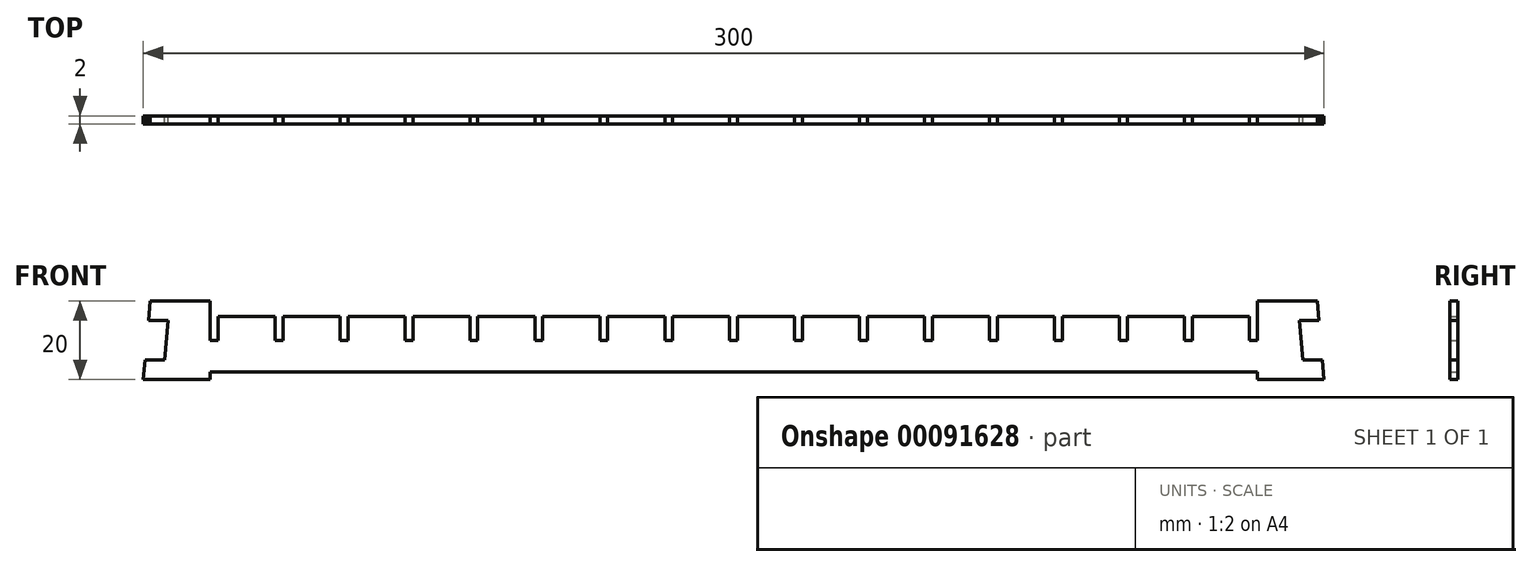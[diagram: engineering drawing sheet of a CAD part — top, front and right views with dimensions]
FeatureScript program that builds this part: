
annotation { "Feature Type Name" : "Feature", "Feature Type Description" : "" }
export const myFeature = defineFeature(function(context is Context, id is Id, definition is map)
    precondition{}
    {
        {
            var Q0;
            Q0=qCreatedBy(makeId("Front.planeOp"),FACE);
            var sketch = newSketch(context, id + "F0", { "sketchPlane" : qUnion([Q0])});
            skLineSegment(sketch, "E0", {"start": v(0, 0) * mm, "end": v(17, 0) * mm});
            skLineSegment(sketch, "E1", {"start": v(300, 0) * mm, "end": v(299.56, 5) * mm});
            skLineSegment(sketch, "E2", {"start": v(283, 20) * mm, "end": v(283, 10) * mm});
            skLineSegment(sketch, "E3", {"start": v(283, 10) * mm, "end": v(281, 10) * mm});
            skLineSegment(sketch, "E4", {"start": v(281, 10) * mm, "end": v(281, 16) * mm});
            skLineSegment(sketch, "E5", {"start": v(281, 16) * mm, "end": v(266.5, 16) * mm});
            skLineSegment(sketch, "E6", {"start": v(266.5, 16) * mm, "end": v(266.5, 10) * mm});
            skLineSegment(sketch, "E7", {"start": v(266.5, 10) * mm, "end": v(264.5, 10) * mm});
            skLineSegment(sketch, "E8", {"start": v(264.5, 10) * mm, "end": v(264.5, 16) * mm});
            skLineSegment(sketch, "E9", {"start": v(264.5, 16) * mm, "end": v(250, 16) * mm});
            skLineSegment(sketch, "E10", {"start": v(233.5, 16) * mm, "end": v(233.5, 10) * mm});
            skLineSegment(sketch, "E11", {"start": v(233.5, 10) * mm, "end": v(231.5, 10) * mm});
            skLineSegment(sketch, "E12", {"start": v(231.5, 10) * mm, "end": v(231.5, 16) * mm});
            skLineSegment(sketch, "E13", {"start": v(231.5, 16) * mm, "end": v(217, 16) * mm});
            skLineSegment(sketch, "E14", {"start": v(217, 16) * mm, "end": v(217, 10) * mm});
            skLineSegment(sketch, "E15", {"start": v(217, 10) * mm, "end": v(215, 10) * mm});
            skLineSegment(sketch, "E16", {"start": v(215, 10) * mm, "end": v(215, 16) * mm});
            skLineSegment(sketch, "E17", {"start": v(215, 16) * mm, "end": v(200.5, 16) * mm});
            skLineSegment(sketch, "E18", {"start": v(200.5, 16) * mm, "end": v(200.5, 10) * mm});
            skLineSegment(sketch, "E19", {"start": v(200.5, 10) * mm, "end": v(198.5, 10) * mm});
            skLineSegment(sketch, "E20", {"start": v(198.5, 10) * mm, "end": v(198.5, 16) * mm});
            skLineSegment(sketch, "E21", {"start": v(198.5, 16) * mm, "end": v(184, 16) * mm});
            skLineSegment(sketch, "E22", {"start": v(184, 16) * mm, "end": v(184, 10) * mm});
            skLineSegment(sketch, "E23", {"start": v(184, 10) * mm, "end": v(182, 10) * mm});
            skLineSegment(sketch, "E24", {"start": v(182, 10) * mm, "end": v(182, 16) * mm});
            skLineSegment(sketch, "E25", {"start": v(182, 16) * mm, "end": v(167.5, 16) * mm});
            skLineSegment(sketch, "E26", {"start": v(167.5, 16) * mm, "end": v(167.5, 10) * mm});
            skLineSegment(sketch, "E27", {"start": v(167.5, 10) * mm, "end": v(165.5, 10) * mm});
            skLineSegment(sketch, "E28", {"start": v(165.5, 10) * mm, "end": v(165.5, 16) * mm});
            skLineSegment(sketch, "E29", {"start": v(165.5, 16) * mm, "end": v(151, 16) * mm});
            skLineSegment(sketch, "E30", {"start": v(151, 16) * mm, "end": v(151, 10) * mm});
            skLineSegment(sketch, "E31", {"start": v(151, 10) * mm, "end": v(149, 10) * mm});
            skLineSegment(sketch, "E32", {"start": v(149, 10) * mm, "end": v(149, 16) * mm});
            skLineSegment(sketch, "E33", {"start": v(149, 16) * mm, "end": v(134.5, 16) * mm});
            skLineSegment(sketch, "E34", {"start": v(134.5, 16) * mm, "end": v(134.5, 10) * mm});
            skLineSegment(sketch, "E35", {"start": v(134.5, 10) * mm, "end": v(132.5, 10) * mm});
            skLineSegment(sketch, "E36", {"start": v(132.5, 10) * mm, "end": v(132.5, 16) * mm});
            skLineSegment(sketch, "E37", {"start": v(132.5, 16) * mm, "end": v(118, 16) * mm});
            skLineSegment(sketch, "E38", {"start": v(118, 16) * mm, "end": v(118, 10) * mm});
            skLineSegment(sketch, "E39", {"start": v(118, 10) * mm, "end": v(116, 10) * mm});
            skLineSegment(sketch, "E40", {"start": v(116, 10) * mm, "end": v(116, 16) * mm});
            skLineSegment(sketch, "E41", {"start": v(116, 16) * mm, "end": v(101.5, 16) * mm});
            skLineSegment(sketch, "E42", {"start": v(101.5, 16) * mm, "end": v(101.5, 10) * mm});
            skLineSegment(sketch, "E43", {"start": v(101.5, 10) * mm, "end": v(99.5, 10) * mm});
            skLineSegment(sketch, "E44", {"start": v(99.5, 10) * mm, "end": v(99.5, 16) * mm});
            skLineSegment(sketch, "E45", {"start": v(99.5, 16) * mm, "end": v(85, 16) * mm});
            skLineSegment(sketch, "E46", {"start": v(85, 16) * mm, "end": v(85, 10) * mm});
            skLineSegment(sketch, "E47", {"start": v(85, 10) * mm, "end": v(83, 10) * mm});
            skLineSegment(sketch, "E48", {"start": v(83, 10) * mm, "end": v(83, 16) * mm});
            skLineSegment(sketch, "E49", {"start": v(83, 16) * mm, "end": v(68.5, 16) * mm});
            skLineSegment(sketch, "E50", {"start": v(68.5, 16) * mm, "end": v(68.5, 10) * mm});
            skLineSegment(sketch, "E51", {"start": v(68.5, 10) * mm, "end": v(66.5, 10) * mm});
            skLineSegment(sketch, "E52", {"start": v(66.5, 10) * mm, "end": v(66.5, 16) * mm});
            skLineSegment(sketch, "E53", {"start": v(66.5, 16) * mm, "end": v(52, 16) * mm});
            skLineSegment(sketch, "E54", {"start": v(52, 16) * mm, "end": v(52, 10) * mm});
            skLineSegment(sketch, "E55", {"start": v(52, 10) * mm, "end": v(50, 10) * mm});
            skLineSegment(sketch, "E56", {"start": v(50, 10) * mm, "end": v(50, 16) * mm});
            skLineSegment(sketch, "E57", {"start": v(50, 16) * mm, "end": v(35.5, 16) * mm});
            skLineSegment(sketch, "E58", {"start": v(35.5, 16) * mm, "end": v(35.5, 10) * mm});
            skLineSegment(sketch, "E59", {"start": v(35.5, 10) * mm, "end": v(33.5, 10) * mm});
            skLineSegment(sketch, "E60", {"start": v(33.5, 10) * mm, "end": v(33.5, 16) * mm});
            skLineSegment(sketch, "E61", {"start": v(33.5, 16) * mm, "end": v(19, 16) * mm});
            skLineSegment(sketch, "E62", {"start": v(19, 16) * mm, "end": v(19, 10) * mm});
            skLineSegment(sketch, "E63", {"start": v(19, 10) * mm, "end": v(17, 10) * mm});
            skLineSegment(sketch, "E64", {"start": v(17, 10) * mm, "end": v(17, 20) * mm});
            skLineSegment(sketch, "E65", {"start": v(1.75, 20) * mm, "end": v(1.31, 15) * mm});
            skLineSegment(sketch, "E66", {"start": v(248, 16) * mm, "end": v(233.5, 16) * mm});
            skLineSegment(sketch, "E67", {"start": v(250, 16) * mm, "end": v(250, 10) * mm});
            skLineSegment(sketch, "E68", {"start": v(250, 10) * mm, "end": v(248, 10) * mm});
            skLineSegment(sketch, "E69", {"start": v(248, 10) * mm, "end": v(248, 16) * mm});
            skLineSegment(sketch, "E70", {"start": v(283, 20) * mm, "end": v(298.25, 20) * mm});
            skLineSegment(sketch, "E71", {"start": v(1.75, 20) * mm, "end": v(17, 20) * mm});
            skLineSegment(sketch, "E72", {"start": v(0.44, 5) * mm, "end": v(0, 0) * mm});
            skLineSegment(sketch, "E73", {"start": v(0.44, 5) * mm, "end": v(5.44, 5) * mm});
            skLineSegment(sketch, "E74", {"start": v(5.44, 5) * mm, "end": v(6.31, 15) * mm});
            skLineSegment(sketch, "E75", {"start": v(6.31, 15) * mm, "end": v(1.31, 15) * mm});
            skLineSegment(sketch, "E76", {"start": v(298.69, 15) * mm, "end": v(298.25, 20) * mm});
            skLineSegment(sketch, "E77", {"start": v(298.69, 15) * mm, "end": v(293.69, 15) * mm});
            skLineSegment(sketch, "E78", {"start": v(293.69, 15) * mm, "end": v(294.56, 5) * mm});
            skLineSegment(sketch, "E79", {"start": v(294.56, 5) * mm, "end": v(299.56, 5) * mm});
            skLineSegment(sketch, "E80", {"start": v(17, 0) * mm, "end": v(17, 2) * mm});
            skLineSegment(sketch, "E81", {"start": v(283, 0) * mm, "end": v(300, 0) * mm});
            skLineSegment(sketch, "E82", {"start": v(283, 2) * mm, "end": v(283, 0) * mm});
            skLineSegment(sketch, "E83", {"start": v(17, 2) * mm, "end": v(283, 2) * mm});
            skSolve(sketch);
        }
        {
            var Q0;
            Q0 = qSketchRegion(id + "F0", true);
            extrude(context, id + "F1", {"entities" : qUnion([Q0]), "depth" : 2 * mm});
        }
    });
